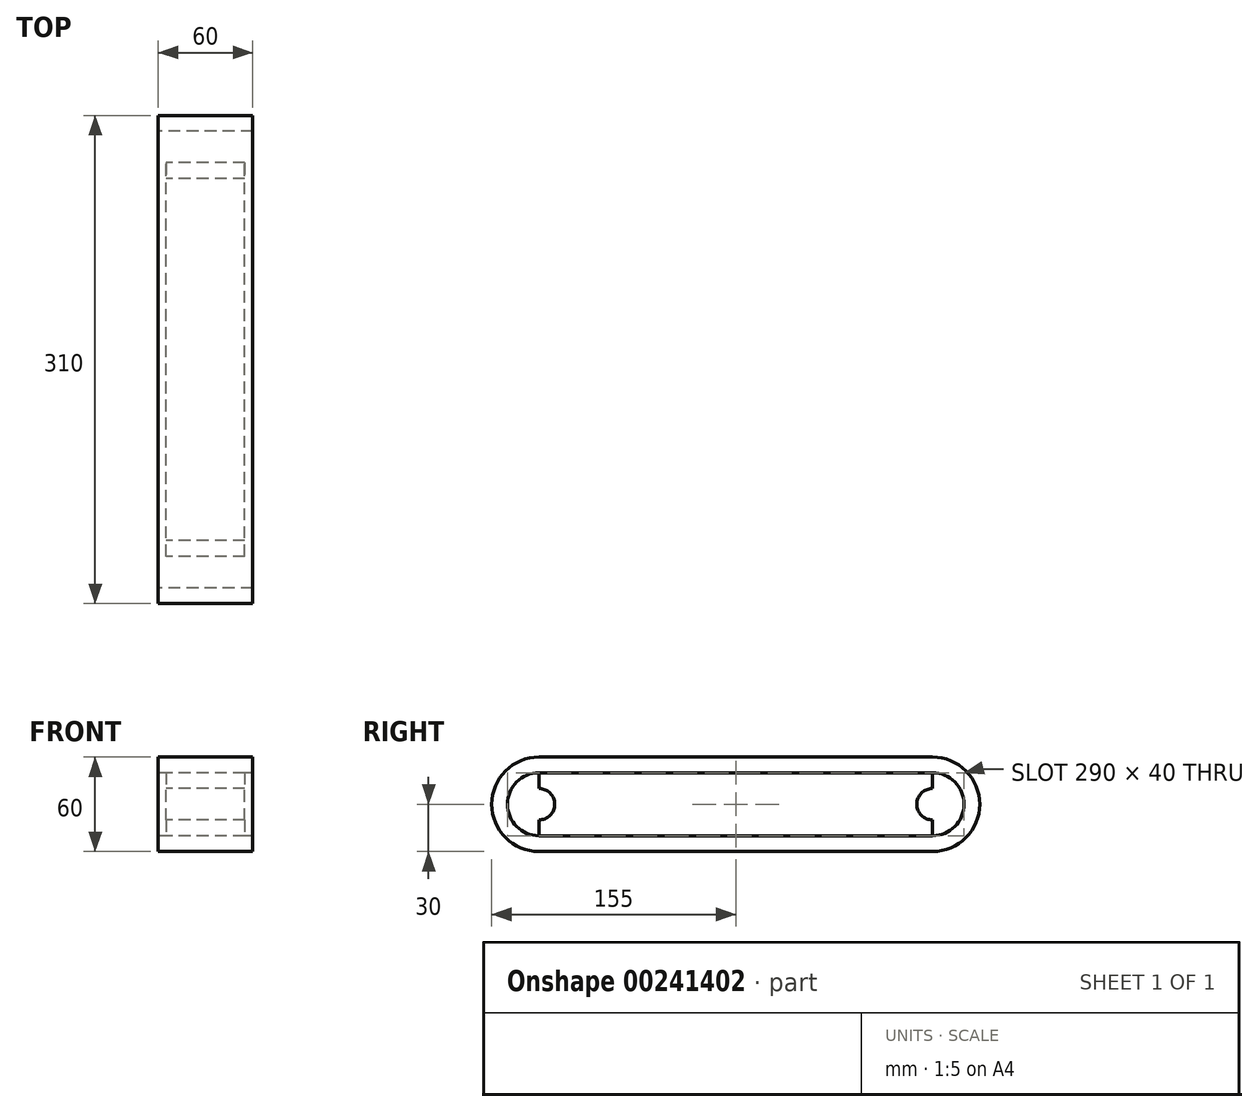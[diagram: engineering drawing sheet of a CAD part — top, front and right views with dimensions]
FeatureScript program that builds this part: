
annotation { "Feature Type Name" : "Feature", "Feature Type Description" : "" }
export const myFeature = defineFeature(function(context is Context, id is Id, definition is map)
    precondition{}
    {
        {
            var Q0;
            Q0=qCreatedBy(makeId("Right.planeOp"),FACE);
            var sketch = newSketch(context, id + "F0", { "sketchPlane" : qUnion([Q0])});
            skLineSegment(sketch, "E0.bottom", {"start": v(-125, 30) * mm, "end": v(125, 30) * mm});
            skLineSegment(sketch, "E0.top", {"start": v(-125, -30) * mm, "end": v(125, -30) * mm});
            skLineSegment(sketch, "E0.left", {"start": v(-125, 30) * mm, "end": v(-125, -30) * mm});
            skLineSegment(sketch, "E0.right", {"start": v(125, 30) * mm, "end": v(125, -30) * mm});
            skPoint(sketch, "E0.middle", {"position": v(0, 0) * mm});
            skLineSegment(sketch, "E1.bottom", {"start": v(-125, 20) * mm, "end": v(125, 20) * mm});
            skLineSegment(sketch, "E1.top", {"start": v(-125, -20) * mm, "end": v(125, -20) * mm});
            skLineSegment(sketch, "E1.left", {"start": v(-125, 20) * mm, "end": v(-125, -20) * mm});
            skLineSegment(sketch, "E1.right", {"start": v(125, 20) * mm, "end": v(125, -20) * mm});
            skArc(sketch, "E2", {"start": v(-125, 30) * mm, "mid": v(-155, 0) * mm, "end": v(-125, -30) * mm});
            skArc(sketch, "E3", {"start": v(125, -30) * mm, "mid": v(155, 0) * mm, "end": v(125, 30) * mm});
            skArc(sketch, "E4", {"start": v(125, -20) * mm, "mid": v(145, 0) * mm, "end": v(125, 20) * mm});
            skArc(sketch, "E5", {"start": v(-125, 20) * mm, "mid": v(-145, 0) * mm, "end": v(-125, -20) * mm});
            skSolve(sketch);
        }
        {
            var Q0;
            Q0 = qSketchRegion(id + "F0", true);
            extrude(context, id + "F1", {"entities" : qUnion([Q0]), "depth" : 60 * mm});
        }
        {
            var Q0;
            Q0=makeQuery(id+"F0.imprint","IMPRINT",FACE,{"disambiguationData":[TD([[makeQuery(id+"F0.imprint","IMPRINT",EDGE,{"derivedFrom":sQuery(id+"F0.wireOp",EDGE,"E1.bottom")}),-1.0]])]});
            var Q1;
            Q1=makeQuery(id+"F0.imprint","IMPRINT",FACE,{"disambiguationData":[TD([[makeQuery(id+"F0.imprint","IMPRINT",EDGE,{"derivedFrom":sQuery(id+"F0.wireOp",EDGE,"E1.right")}),1.0]])]});
            var Q2;
            Q2=makeQuery(id+"F0.imprint","IMPRINT",FACE,{"disambiguationData":[TD([[makeQuery(id+"F0.imprint","IMPRINT",EDGE,{"derivedFrom":sQuery(id+"F0.wireOp",EDGE,"E1.left")}),-1.0]])]});
            extrude(context, id + "F2", {"entities" : qUnion([Q0, Q1, Q2]), "operationType" : NewBodyOperationType.ADD, "depth" : 55 * mm, "hasSecondDirection" : true, "secondDirectionOppositeDirection" : true, "secondDirectionDepth" : -5 * mm});
        }
        {
            var Q0;
            Q0=qCreatedBy(makeId("Right.planeOp"),FACE);
            var sketch = newSketch(context, id + "F3", { "sketchPlane" : qUnion([Q0])});
            skCircle(sketch, "E6", {"center": v(-125, 0) * mm, "radius": 10 * mm});
            skCircle(sketch, "E7", {"center": v(125, 0) * mm, "radius": 10 * mm});
            skSolve(sketch);
        }
        {
            var Q0;
            Q0 = qSketchRegion(id + "F3", true);
            extrude(context, id + "F4", {"entities" : qUnion([Q0]), "operationType" : NewBodyOperationType.REMOVE, "endBound" : BoundingType.THROUGH_ALL, "depth" : 25 * mm});
        }
    });
